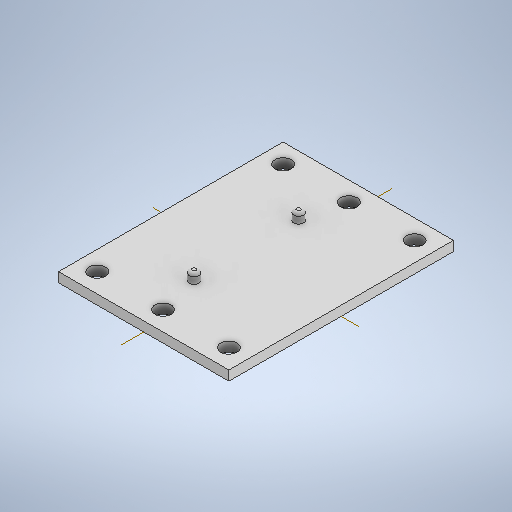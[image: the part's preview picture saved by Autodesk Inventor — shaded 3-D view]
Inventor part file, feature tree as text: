
AUTODESK INVENTOR PART (.ipt)
format: ipt  version: 2025 (Build 290162000, 162)  size: 254,464 bytes
history: native  units: mm
features: sketch x3, extrude x2, hole x1, pattern_linear x1, mirror x1, fillet x1
ambient origin geometry x8: Origin, YZ Plane, XZ Plane, XY Plane, X Axis, Y Axis, Z Axis, Center Point
bodies: Solid1 (feature_tree)
feature tree (9):
  extrude  "Extrusion1"  Depth=58.0mm
  hole  "Hole1"  [1 undecoded]
  pattern_linear  "Rectangular Pattern1"  Count1=2 Spacing1=17.0mm
  mirror  "Mirror1"
  extrude  "Extrusion2"  Depth=0.75mm
  fillet  "Fillet1"  Radius=2.5mm
  sketch  "Sketch1"  dims[d2=44.0mm d3=58.0mm]
  sketch  "Sketch2"  dims[d13=2.5mm d14=0.0mm]
  sketch  "Sketch3"  dims[d15=4.2mm d16=6.0mm d17=4.0mm d18=2.0mm d19=90.0deg d20=8.0mm d21=20.594885mm d22=5.0mm d23=20.0mm d25=17.0mm d26=20.0mm d28=17.0mm d29=2.5mm d30=2.5mm d31=13.5mm d32=2.5mm d33=0.0mm d34=0.75mm]
note: 1 required parameter value undecoded (feature->parameter linkage not recoverable at this tier; creation-order binding heuristic only, values carry confidence <= 0.55)
